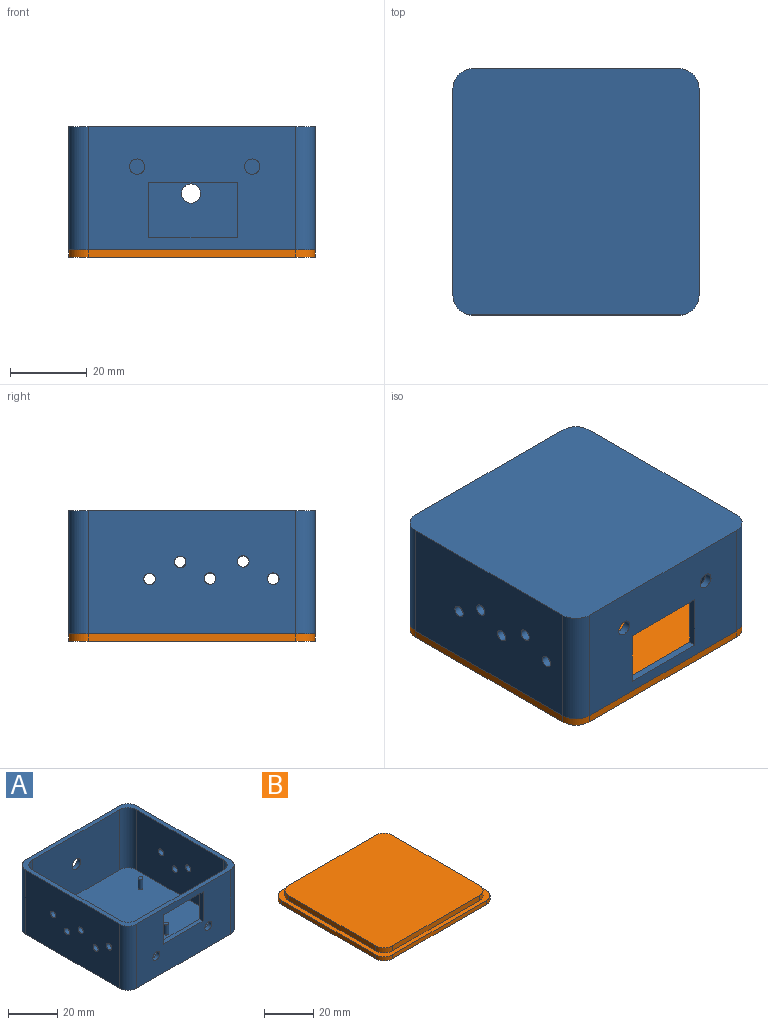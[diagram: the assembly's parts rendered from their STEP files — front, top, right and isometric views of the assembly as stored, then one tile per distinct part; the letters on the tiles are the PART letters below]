
ASSEMBLY  parts=2 mates=1
PART A: 44 faces, bbox 64x64x32 mm
  f0: plane 54x32mm, normal (0,-1,0), area 1369.4mm2, adj f2,f6,f19,f20,f27,f28,f40,f41
  f1: plane 50x30mm, normal (0,1,0), area 1141.4mm2, adj f2,f10,f19,f20,f22,f24,f40,f41
  f2: plane 64x64mm, normal (0,0,1), area 496mm2, adj f0,f1,f3,f4,f5,f7,f8,f9
  f3: plane 54x32mm, normal (0,1,0), area 1708.4mm2, adj f2,f6,f21,f26,f29
  f4: plane 54x32mm, normal (-1,0,0), area 1692.7mm2, adj f2,f6,f26,f27,f30,f31,f32,f33
  f5: plane 54x32mm, normal (1,0,0), area 1692.7mm2, adj f2,f6,f28,f29,f35,f36,f37,f38
  f6: plane 64x64mm, normal (0,0,-1), area 4074.5mm2, adj f0,f3,f4,f5,f26,f27,f28,f29
  f7: plane 50x30mm, normal (0,-1,0), area 1480.4mm2, adj f2,f10,f21,f23,f25
  f8: plane 50x30mm, normal (1,0,0), area 1464.7mm2, adj f2,f10,f24,f25,f30,f31,f32,f33
  f9: plane 50x30mm, normal (-1,0,0), area 1464.7mm2, adj f2,f10,f22,f23,f35,f36,f37,f38
  f10: plane 60x60mm, normal (0,0,1), area 3566mm2, adj f1,f7,f8,f9,f11,f13,f15,f17
  f11: cylinder r=1mm len=5mm, axis (0,0,-1), area 31.4mm2, adj f10,f12
  f12: plane 2x2mm, normal (0,0,1), area 3.1mm2, adj f11
  f13: cylinder r=1mm len=5mm, axis (0,0,-1), area 31.4mm2, adj f10,f14
  f14: plane 2x2mm, normal (0,0,1), area 3.1mm2, adj f13
  f15: cylinder r=1mm len=5mm, axis (0,0,-1), area 31.4mm2, adj f10,f16
  f16: plane 2x2mm, normal (0,0,1), area 3.1mm2, adj f15
  f17: cylinder r=1mm len=5mm, axis (0,0,-1), area 31.4mm2, adj f10,f18
  f18: plane 2x2mm, normal (0,0,1), area 3.1mm2, adj f17
  f19: cylinder r=2mm len=4mm, axis (0,-1,0), area 25.1mm2, adj f0,f1
  f20: cylinder r=2mm len=4mm, axis (0,-1,0), area 25.1mm2, adj f0,f1
  f21: cylinder r=2.5mm len=5mm, axis (0,1,0), area 31.4mm2, adj f3,f7
  f22: cylinder r=5mm len=30mm, axis (0,0,-1), area 235.6mm2, adj f1,f2,f9,f10
  f23: cylinder r=5mm len=30mm, axis (0,0,1), area 235.6mm2, adj f2,f7,f9,f10
  f24: cylinder r=5mm len=30mm, axis (0,0,1), area 235.6mm2, adj f1,f2,f8,f10
  f25: cylinder r=5mm len=30mm, axis (0,0,-1), area 235.6mm2, adj f2,f7,f8,f10
  f26: cylinder r=5mm len=32mm, axis (0,0,1), area 251.3mm2, adj f2,f3,f4,f6
  f27: cylinder r=5mm len=32mm, axis (0,0,-1), area 251.3mm2, adj f0,f2,f4,f6
  f28: cylinder r=5mm len=32mm, axis (0,0,1), area 251.3mm2, adj f0,f2,f5,f6
  f29: cylinder r=5mm len=32mm, axis (0,0,-1), area 251.3mm2, adj f2,f3,f5,f6
  f30: cylinder r=1.5mm len=3mm, axis (-1,0,0), area 18.8mm2, adj f4,f8
  f31: cylinder r=1.5mm len=3mm, axis (-1,0,0), area 18.8mm2, adj f4,f8
  f32: cylinder r=1.5mm len=3mm, axis (-1,0,0), area 18.8mm2, adj f4,f8
  f33: cylinder r=1.5mm len=3mm, axis (-1,0,0), area 18.8mm2, adj f4,f8
  f34: cylinder r=1.5mm len=3mm, axis (-1,0,0), area 18.8mm2, adj f4,f8
  f35: cylinder r=1.5mm len=3mm, axis (1,0,0), area 18.8mm2, adj f5,f9
  f36: cylinder r=1.5mm len=3mm, axis (1,0,0), area 18.8mm2, adj f5,f9
  f37: cylinder r=1.5mm len=3mm, axis (1,0,0), area 18.8mm2, adj f5,f9
  f38: cylinder r=1.5mm len=3mm, axis (1,0,0), area 18.8mm2, adj f5,f9
  f39: cylinder r=1.5mm len=3mm, axis (1,0,0), area 18.8mm2, adj f5,f9
  f40: plane 23x2mm, normal (0,0,-1), area 46mm2, adj f0,f1,f41,f43
  f41: plane 14.5x2mm, normal (1,0,0), area 29mm2, adj f0,f1,f40,f42
  f42: plane 23x2mm, normal (0,0,1), area 46mm2, adj f0,f1,f41,f43
  f43: plane 14.5x2mm, normal (-1,0,0), area 29mm2, adj f0,f1,f40,f42
PART B: 19 faces, bbox 64x64x4.5 mm
  f0: plane 54x2mm, normal (-1,0,0), area 108mm2, adj f4,f5,f15,f18
  f1: plane 54x2mm, normal (0,-1,0), area 108mm2, adj f4,f5,f15,f16
  f2: plane 54x2mm, normal (1,0,0), area 108mm2, adj f4,f5,f16,f17
  f3: plane 54x2mm, normal (0,1,0), area 108mm2, adj f4,f5,f17,f18
  f4: plane 64x64mm, normal (0,0,1), area 496mm2, adj f0,f1,f2,f3,f6,f7,f8,f9
  f5: plane 64x64mm, normal (0,0,-1), area 4074.5mm2, adj f0,f1,f2,f3,f15,f16,f17,f18
  f6: plane 50x2.5mm, normal (-1,0,0), area 125mm2, adj f4,f10,f11,f14
  f7: plane 50x2.5mm, normal (0,-1,0), area 125mm2, adj f4,f10,f11,f12
  f8: plane 50x2.5mm, normal (1,0,0), area 125mm2, adj f4,f10,f12,f13
  f9: plane 50x2.5mm, normal (0,1,0), area 125mm2, adj f4,f10,f13,f14
  f10: plane 60x60mm, normal (0,0,1), area 3578.5mm2, adj f6,f7,f8,f9,f11,f12,f13,f14
  f11: cylinder r=5mm len=5mm, axis (0,0,-1), area 19.6mm2, adj f4,f6,f7,f10
  f12: cylinder r=5mm len=5mm, axis (0,0,-1), area 19.6mm2, adj f4,f7,f8,f10
  f13: cylinder r=5mm len=5mm, axis (0,0,-1), area 19.6mm2, adj f4,f8,f9,f10
  f14: cylinder r=5mm len=5mm, axis (0,0,-1), area 19.6mm2, adj f4,f6,f9,f10
  f15: cylinder r=5mm len=5mm, axis (0,0,-1), area 15.7mm2, adj f0,f1,f4,f5
  f16: cylinder r=5mm len=5mm, axis (0,0,1), area 15.7mm2, adj f1,f2,f4,f5
  f17: cylinder r=5mm len=5mm, axis (0,0,-1), area 15.7mm2, adj f2,f3,f4,f5
  f18: cylinder r=5mm len=5mm, axis (0,0,1), area 15.7mm2, adj f0,f3,f4,f5
PLACE A rot(axis=(0,1,0),180deg) t=(1.69,-29.77,-2.13)mm fixed
PLACE B t=(-2.35,-30.32,-34.13)mm
MATE slider B.f15 <-> A.f28  axis (0,0,1) through (9.56,-17.41,-32.13)mm
